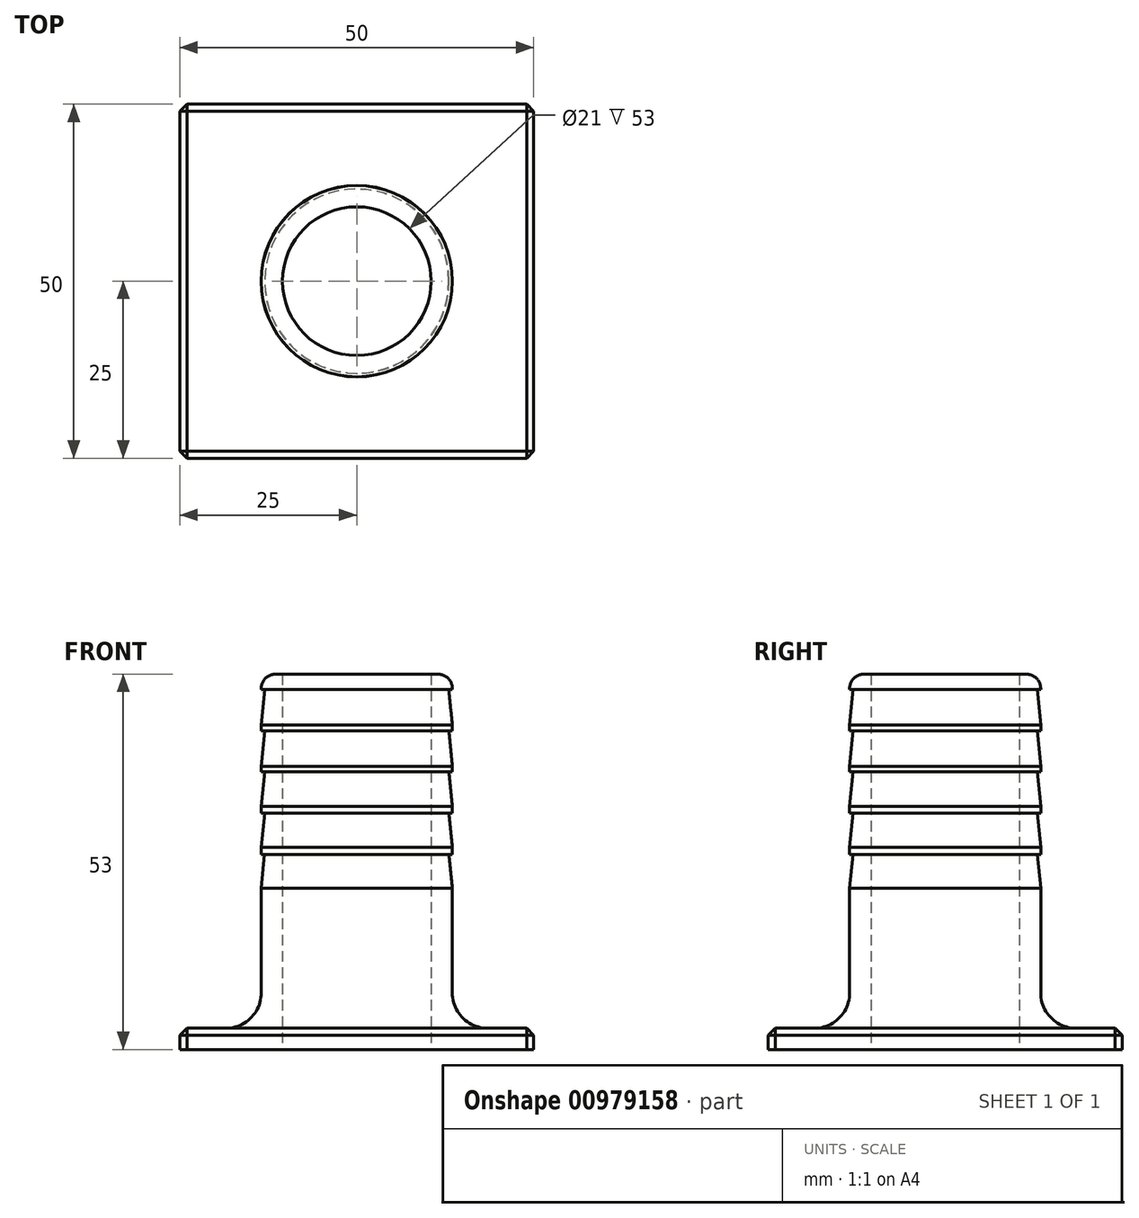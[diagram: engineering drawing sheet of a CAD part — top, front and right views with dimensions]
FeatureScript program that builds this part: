
annotation { "Feature Type Name" : "Feature", "Feature Type Description" : "" }
export const myFeature = defineFeature(function(context is Context, id is Id, definition is map)
    precondition{}
    {
        {
            var Q0;
            Q0=qCreatedBy(makeId("Top.planeOp"),FACE);
            var sketch = newSketch(context, id + "F0", { "sketchPlane" : qUnion([Q0])});
            skLineSegment(sketch, "E0.bottom", {"start": v(-25, 25) * mm, "end": v(25, 25) * mm});
            skLineSegment(sketch, "E0.top", {"start": v(-25, -25) * mm, "end": v(25, -25) * mm});
            skLineSegment(sketch, "E0.left", {"start": v(-25, 25) * mm, "end": v(-25, -25) * mm});
            skLineSegment(sketch, "E0.right", {"start": v(25, 25) * mm, "end": v(25, -25) * mm});
            skCircle(sketch, "E1", {"center": v(0, 0) * mm, "radius": 10.5 * mm});
            skSolve(sketch);
        }
        {
            var Q0;
            Q0=makeQuery(id+"F0.imprint","IMPRINT",FACE,{"disambiguationData":[TD([[makeQuery(id+"F0.imprint","IMPRINT",EDGE,{"derivedFrom":sQuery(id+"F0.wireOp",EDGE,"E0.bottom")}),-1.0]])]});
            extrude(context, id + "F1", {"entities" : qUnion([Q0]), "depth" : 3 * mm, "offsetDistance" : 25 * mm});
        }
        {
            var Q0;
            Q0=qCreatedBy(makeId("Front.planeOp"),FACE);
            var sketch = newSketch(context, id + "F2", { "sketchPlane" : qUnion([Q0])});
            skLineSegment(sketch, "E2.left", {"start": v(-10.5, 53) * mm, "end": v(-10.5, 3) * mm});
            skLineSegment(sketch, "E3.bottom", {"start": v(-10.5, 53) * mm, "end": v(-13.5, 53) * mm});
            skLineSegment(sketch, "E3.right", {"start": v(-13.5, 53) * mm, "end": v(-13.5, 50.84) * mm});
            skLineSegment(sketch, "E4.bottom", {"start": v(-13.5, 50.84) * mm, "end": v(-13, 50.84) * mm});
            skLineSegment(sketch, "E5", {"start": v(-13.5, 45.82) * mm, "end": v(-13, 50.84) * mm});
            skLineSegment(sketch, "E6.1.0.0", {"start": v(-13.5, 40) * mm, "end": v(-13, 45.02) * mm});
            skLineSegment(sketch, "E6.1.0.1", {"start": v(-13.5, 45.02) * mm, "end": v(-13, 45.02) * mm});
            skLineSegment(sketch, "E6.2.0.0", {"start": v(-13.51, 34.17) * mm, "end": v(-13.01, 39.2) * mm});
            skLineSegment(sketch, "E6.2.0.1", {"start": v(-13.51, 39.2) * mm, "end": v(-13.01, 39.2) * mm});
            skLineSegment(sketch, "E6.3.0.0", {"start": v(-13.5, 28.55) * mm, "end": v(-13.02, 33.37) * mm});
            skLineSegment(sketch, "E6.3.0.1", {"start": v(-13.52, 33.37) * mm, "end": v(-13.02, 33.37) * mm});
            skLineSegment(sketch, "E6.4.0.0", {"start": v(-13.53, 22.53) * mm, "end": v(-13.03, 27.55) * mm});
            skLineSegment(sketch, "E6.4.0.1", {"start": v(-13.5, 27.55) * mm, "end": v(-13.03, 27.55) * mm});
            skLineSegment(sketch, "E7.trimOffspring", {"start": v(-13.5, 34.3) * mm, "end": v(-13.5, 33.37) * mm});
            skLineSegment(sketch, "E8", {"start": v(-13.5, 45.82) * mm, "end": v(-13.5, 45.02) * mm});
            skLineSegment(sketch, "E9", {"start": v(-13.5, 40) * mm, "end": v(-13.51, 39.2) * mm});
            skLineSegment(sketch, "E10.trimOffspring", {"start": v(-13.5, 28.55) * mm, "end": v(-13.5, 27.55) * mm});
            skLineSegment(sketch, "E11.trimOffspring", {"start": v(-13.5, 22.8) * mm, "end": v(-13.5, 8) * mm});
            skLineSegment(sketch, "E12", {"start": v(0, 59.85) * mm, "end": v(0, -26.78) * mm});
            skPoint(sketch, "E13.visualSharp", {"position": v(-13.5, 3) * mm});
            skArc(sketch, "E13.filletArc", {"start": v(-18.5, 3) * mm, "mid": v(-14.96, 4.46) * mm, "end": v(-13.5, 8) * mm});
            skPoint(sketch, "E14.end.orphan", {"position": v(-21.5, 3) * mm});
            skLineSegment(sketch, "E15", {"start": v(-18.5, 3) * mm, "end": v(-10.5, 3) * mm});
            skSolve(sketch);
        }
        {
            var Q0;
            Q0 = qSketchRegion(id + "F2", true);
            var Q1;
            Q1=sQuery(id+"F2.wireOp",EDGE,"E12");
            revolve(context, id + "F3", {"operationType" : NewBodyOperationType.ADD, "surfaceOperationType" : NewSurfaceOperationType.NEW, "entities" : qUnion([Q0]), "axis" : qUnion([Q1]), "revolveType" : RevolveType.FULL});
        }
        {
            var Q0;
            Q0=makeQuery(id+"F3.opRevolve","SWEPT_EDGE",EDGE,{"disambiguationData":[OSD([sQuery(id+"F2.wireOp",EDGE,"E3.bottom"),sQuery(id+"F2.wireOp",EDGE,"E3.right")])]});
            fillet(context, id + "F4", {"entities" : qUnion([Q0]), "radius" : 2 * mm, "tangentPropagation" : true, "allowEdgeOverflow" : false});
        }
        {
            var Q0;
            Q0=makeQuery(id+"F1.opExtrude","CAP_EDGE",EDGE,{"disambiguationData":[OSD([sQuery(id+"F0.wireOp",EDGE,"E0.left")])],"isStart":false});
            var Q1;
            Q1=makeQuery(id+"F1.opExtrude","CAP_EDGE",EDGE,{"disambiguationData":[OSD([sQuery(id+"F0.wireOp",EDGE,"E0.top")])],"isStart":false});
            var Q2;
            Q2=makeQuery(id+"F1.opExtrude","CAP_EDGE",EDGE,{"disambiguationData":[OSD([sQuery(id+"F0.wireOp",EDGE,"E0.right")])],"isStart":false});
            var Q3;
            Q3=makeQuery(id+"F1.opExtrude","CAP_EDGE",EDGE,{"disambiguationData":[OSD([sQuery(id+"F0.wireOp",EDGE,"E0.bottom")])],"isStart":false});
            var Q4;
            Q4=makeQuery(id+"F1.opExtrude","SWEPT_EDGE",EDGE,{"disambiguationData":[OSD([sQuery(id+"F0.wireOp",EDGE,"E0.top"),sQuery(id+"F0.wireOp",EDGE,"E0.left")])]});
            var Q5;
            Q5=makeQuery(id+"F1.opExtrude","SWEPT_EDGE",EDGE,{"disambiguationData":[OSD([sQuery(id+"F0.wireOp",EDGE,"E0.top"),sQuery(id+"F0.wireOp",EDGE,"E0.right")])]});
            var Q6;
            Q6=makeQuery(id+"F1.opExtrude","SWEPT_EDGE",EDGE,{"disambiguationData":[OSD([sQuery(id+"F0.wireOp",EDGE,"E0.bottom"),sQuery(id+"F0.wireOp",EDGE,"E0.right")])]});
            var Q7;
            Q7=makeQuery(id+"F1.opExtrude","SWEPT_EDGE",EDGE,{"disambiguationData":[OSD([sQuery(id+"F0.wireOp",EDGE,"E0.bottom"),sQuery(id+"F0.wireOp",EDGE,"E0.left")])]});
            chamfer(context, id + "F5", {"entities" : qUnion([Q0, Q1, Q2, Q3, Q4, Q5, Q6, Q7]), "width" : 1 * mm, "tangentPropagation" : true});
        }
    });
